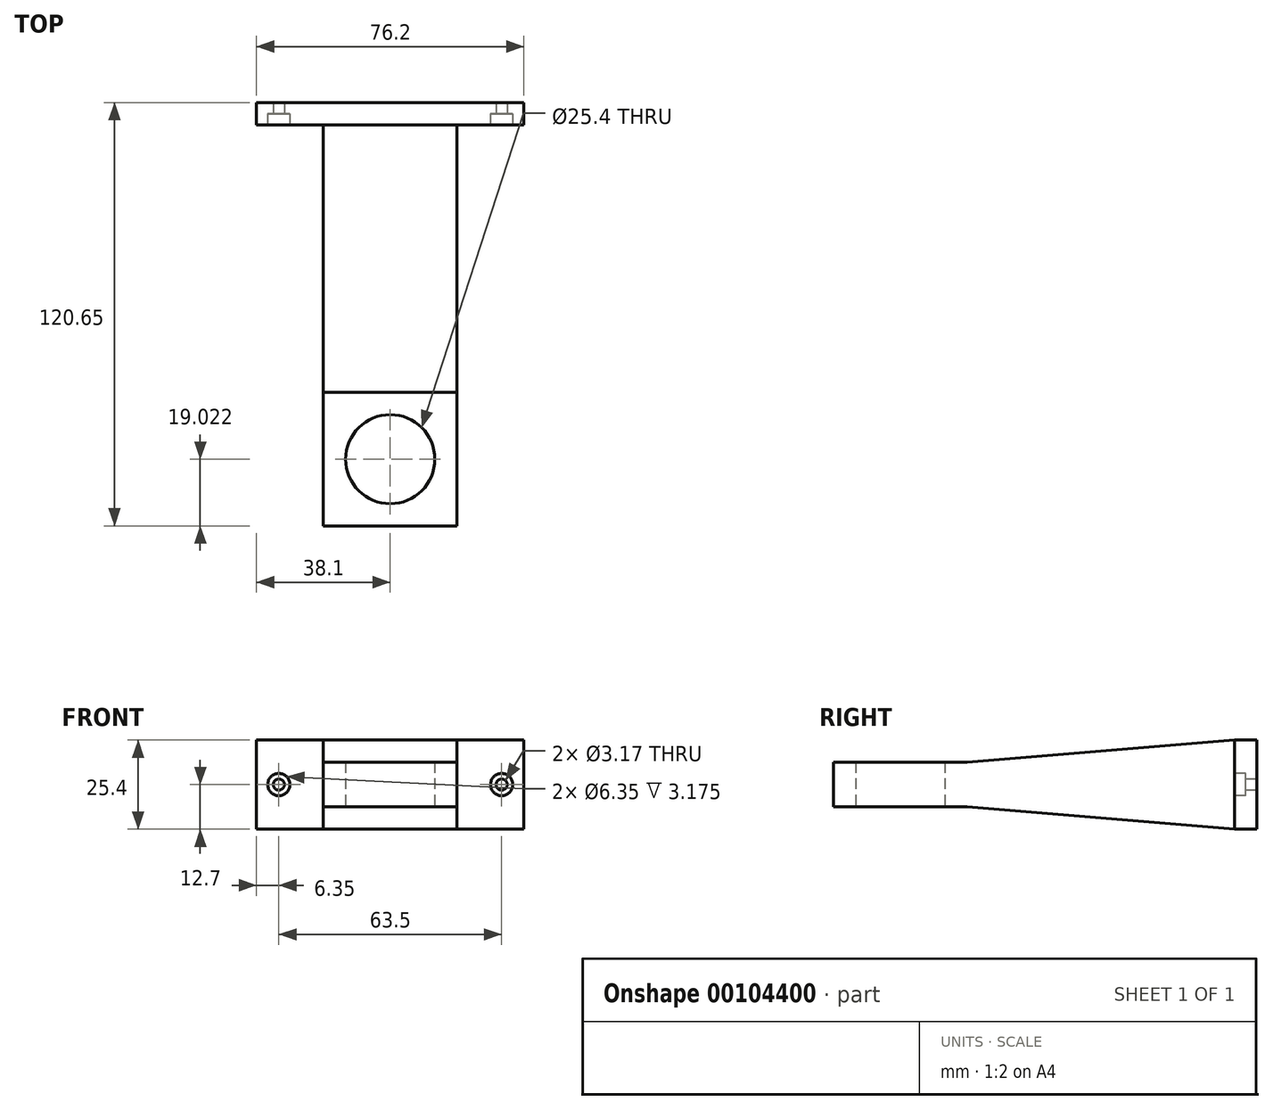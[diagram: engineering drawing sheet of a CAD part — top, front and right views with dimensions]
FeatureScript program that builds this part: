
annotation { "Feature Type Name" : "Feature", "Feature Type Description" : "" }
export const myFeature = defineFeature(function(context is Context, id is Id, definition is map)
    precondition{}
    {
        {
            var Q0;
            Q0=qCreatedBy(makeId("Front.planeOp"),FACE);
            var sketch = newSketch(context, id + "F0", { "sketchPlane" : qUnion([Q0])});
            skLineSegment(sketch, "E0.bottom", {"start": v(0, 0) * mm, "end": v(76.2, 0) * mm});
            skLineSegment(sketch, "E0.top", {"start": v(0, 25.4) * mm, "end": v(76.2, 25.4) * mm});
            skLineSegment(sketch, "E0.left", {"start": v(0, 0) * mm, "end": v(0, 25.4) * mm});
            skLineSegment(sketch, "E0.right", {"start": v(76.2, 0) * mm, "end": v(76.2, 25.4) * mm});
            skSolve(sketch);
        }
        {
            var Q0;
            Q0 = qSketchRegion(id + "F0", true);
            extrude(context, id + "F1", {"entities" : qUnion([Q0]), "depth" : 6.35 * mm});
        }
        {
            var Q0;
            Q0=makeQuery(id+"F1.opExtrude","CAP_FACE",FACE,{"disambiguationData":[OSD([sQuery(id+"F0.wireOp",EDGE,"E0.bottom"),sQuery(id+"F0.wireOp",EDGE,"E0.top"),sQuery(id+"F0.wireOp",EDGE,"E0.left"),sQuery(id+"F0.wireOp",EDGE,"E0.right")])],"isStart":false});
            var sketch = newSketch(context, id + "F2", { "sketchPlane" : qUnion([Q0])});
            skPoint(sketch, "E1", {"position": v(6.35, 12.7) * mm});
            skPoint(sketch, "E2", {"position": v(69.85, 12.7) * mm});
            skSolve(sketch);
        }
        {
            var Q0;
            Q0=sQuery(id+"F2.wireOp",VERTEX,"E1");
            var Q1;
            Q1=sQuery(id+"F2.wireOp",VERTEX,"E2");
            var Q2;
            Q2=makeQuery(id+"F1.opExtrude","SWEPT_BODY",BODY,{"disambiguationData":[OSD([sQuery(id+"F0.wireOp",EDGE,"E0.bottom"),sQuery(id+"F0.wireOp",EDGE,"E0.top"),sQuery(id+"F0.wireOp",EDGE,"E0.left"),sQuery(id+"F0.wireOp",EDGE,"E0.right")])]});
            hole(context, id + "F3", {"style" : HoleStyle.C_BORE, "endStyle" : HoleEndStyle.THROUGH, "holeDiameter" : 3.17 * mm, "cBoreDiameter" : 6.35 * mm, "cBoreDepth" : 3.17 * mm, "locations" : qUnion([Q0, Q1]), "scope" : qUnion([Q2]), "isTappedThrough" : true});
        }
        {
            var Q0;
            Q0=makeQuery(id+"F1.opExtrude","CAP_FACE",FACE,{"disambiguationData":[OSD([sQuery(id+"F0.wireOp",EDGE,"E0.bottom"),sQuery(id+"F0.wireOp",EDGE,"E0.top"),sQuery(id+"F0.wireOp",EDGE,"E0.left"),sQuery(id+"F0.wireOp",EDGE,"E0.right")])],"isStart":false});
            var sketch = newSketch(context, id + "F4", { "sketchPlane" : qUnion([Q0])});
            skLineSegment(sketch, "E3.bottom", {"start": v(19.05, 0) * mm, "end": v(57.15, 0) * mm});
            skLineSegment(sketch, "E3.top", {"start": v(19.05, 25.4) * mm, "end": v(57.15, 25.4) * mm});
            skLineSegment(sketch, "E3.left", {"start": v(19.05, 0) * mm, "end": v(19.05, 25.4) * mm});
            skLineSegment(sketch, "E3.right", {"start": v(57.15, 0) * mm, "end": v(57.15, 25.4) * mm});
            skSolve(sketch);
        }
        {
            var Q0;
            Q0=makeQuery(id+"F4.imprint","IMPRINT",FACE,{"disambiguationData":[TD([[makeQuery(id+"F4.imprint","IMPRINT",EDGE,{"derivedFrom":sQuery(id+"F4.wireOp",EDGE,"E3.bottom")}),1.0]])]});
            cPlane(context, id + "F5", {"entities" : qUnion([Q0]), "cplaneType" : CPlaneType.OFFSET, "offset" : 76.2 * mm, "width" : 152.4 * mm, "height" : 152.4 * mm});
        }
        {
            var Q0;
            Q0=qCreatedBy(id+"F5.planeOp",FACE);
            var sketch = newSketch(context, id + "F6", { "sketchPlane" : qUnion([Q0])});
            skLineSegment(sketch, "E4.0", {"start": v(57.15, 6.35) * mm, "end": v(57.15, 19.05) * mm});
            skLineSegment(sketch, "E5.0", {"start": v(19.05, 6.35) * mm, "end": v(19.05, 19.05) * mm});
            skLineSegment(sketch, "E6", {"start": v(19.05, 19.05) * mm, "end": v(57.15, 19.05) * mm});
            skLineSegment(sketch, "E7", {"start": v(19.05, 6.35) * mm, "end": v(57.15, 6.35) * mm});
            skPoint(sketch, "E8.0.end.orphan", {"position": v(57.15, 0) * mm});
            skPoint(sketch, "E8.0.start.orphan", {"position": v(19.05, 0) * mm});
            skPoint(sketch, "E9.orphan", {"position": v(57.15, 25.4) * mm});
            skPoint(sketch, "E10.0.start.orphan", {"position": v(19.05, 25.4) * mm});
            skSolve(sketch);
        }
        {
            var Q1;
            Q1=makeQuery(id+"F4.imprint","IMPRINT",FACE,{"disambiguationData":[TD([[makeQuery(id+"F4.imprint","IMPRINT",EDGE,{"derivedFrom":sQuery(id+"F4.wireOp",EDGE,"E3.bottom")}),1.0]])]});
            var Q2;
            Q2=makeQuery(id+"F6.imprint","IMPRINT",FACE,{"disambiguationData":[TD([[makeQuery(id+"F6.imprint","IMPRINT",EDGE,{"derivedFrom":sQuery(id+"F6.wireOp",EDGE,"E4.0")}),1.0]])]});
            loft(context, id + "F7", {"operationType" : NewBodyOperationType.ADD, "sheetProfilesArray" : [{ "sheetProfileEntities" : qUnion([Q1]) }, { "sheetProfileEntities" : qUnion([Q2]) }]});
        }
        {
            var Q0;
            Q0=makeQuery(id+"F7.opLoft","CAP_FACE",FACE,{"disambiguationData":[OSD([makeQuery(id+"F6.imprint","IMPRINT",FACE,{"disambiguationData":[TD([[makeQuery(id+"F6.imprint","IMPRINT",EDGE,{"derivedFrom":sQuery(id+"F6.wireOp",EDGE,"E4.0")}),1.0]])]})])],"isStart":true});
            var sketch = newSketch(context, id + "F8", { "sketchPlane" : qUnion([Q0])});
            skSolve(sketch);
        }
        {
            var Q0;
            Q0 = qSketchRegion(id + "F8", true);
            var Q1;
            {var subQ0=sQuery(id+"F6.wireOp",EDGE,"E7");var subQ1=sQuery(id+"F6.wireOp",EDGE,"E6");var subQ2=sQuery(id+"F6.wireOp",EDGE,"E4.0");Q1=makeQuery(id+"F8.imprint","IMPRINT",FACE,{"disambiguationData":[TD([[makeQuery(id+"F8.imprint","IMPRINT",EDGE,{"derivedFrom":makeQuery(id+"F7.opLoft","MID_CAP_EDGE",EDGE,{"disambiguationData":[OSD([subQ2,subQ1,subQ0])],"capPos":1.0})}),1.0]])]});}
            extrude(context, id + "F9", {"entities" : qUnion([Q0, Q1]), "operationType" : NewBodyOperationType.ADD, "depth" : 38.1 * mm});
        }
        {
            var Q0;
            Q0=makeQuery(id+"F9.opExtrude","SWEPT_FACE",FACE,{"disambiguationData":[OSD([sQuery(id+"F6.wireOp",EDGE,"E4.0"),sQuery(id+"F6.wireOp",EDGE,"E5.0"),sQuery(id+"F6.wireOp",EDGE,"E7")])]});
            var sketch = newSketch(context, id + "F10", { "sketchPlane" : qUnion([Q0])});
            skPoint(sketch, "E11", {"position": v(38.1, 120.65) * mm});
            skPoint(sketch, "E12", {"position": v(57.15, 101.6) * mm});
            skPoint(sketch, "E13", {"position": v(38.1, 101.63) * mm});
            skSolve(sketch);
        }
        {
            var Q0;
            Q0=sQuery(id+"F10.wireOp",VERTEX,"E13");
            var Q1;
            Q1=makeQuery(id+"F1.opExtrude","SWEPT_BODY",BODY,{"disambiguationData":[OSD([sQuery(id+"F0.wireOp",EDGE,"E0.bottom"),sQuery(id+"F0.wireOp",EDGE,"E0.top"),sQuery(id+"F0.wireOp",EDGE,"E0.left"),sQuery(id+"F0.wireOp",EDGE,"E0.right")])]});
            hole(context, id + "F11", {"style" : HoleStyle.SIMPLE, "endStyle" : HoleEndStyle.THROUGH, "holeDiameter" : 25.4 * mm, "locations" : qUnion([Q0]), "scope" : qUnion([Q1]), "isTappedThrough" : true});
        }
    });
